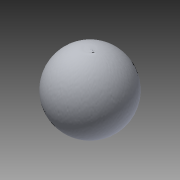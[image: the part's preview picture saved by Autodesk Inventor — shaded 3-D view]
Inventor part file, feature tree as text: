
AUTODESK INVENTOR PART (.ipt)
format: ipt  version: 2013 (Build 170138000, 138)  size: 99,328 bytes
history: native  units: mm
features: revolve x1, sketch x1
ambient origin geometry x8: Origin, YZ Plane, XZ Plane, XY Plane, X Axis, Y Axis, Z Axis, Center Point
bodies: Solid1 (feature_tree)
feature tree (2):
  revolve  "Revolution1"  [1 undecoded]
  sketch  "Sketch1"  dims[d0=90.0deg d1=40.0mm]
note: 1 required parameter value undecoded (feature->parameter linkage not recoverable at this tier; creation-order binding heuristic only, values carry confidence <= 0.55)
